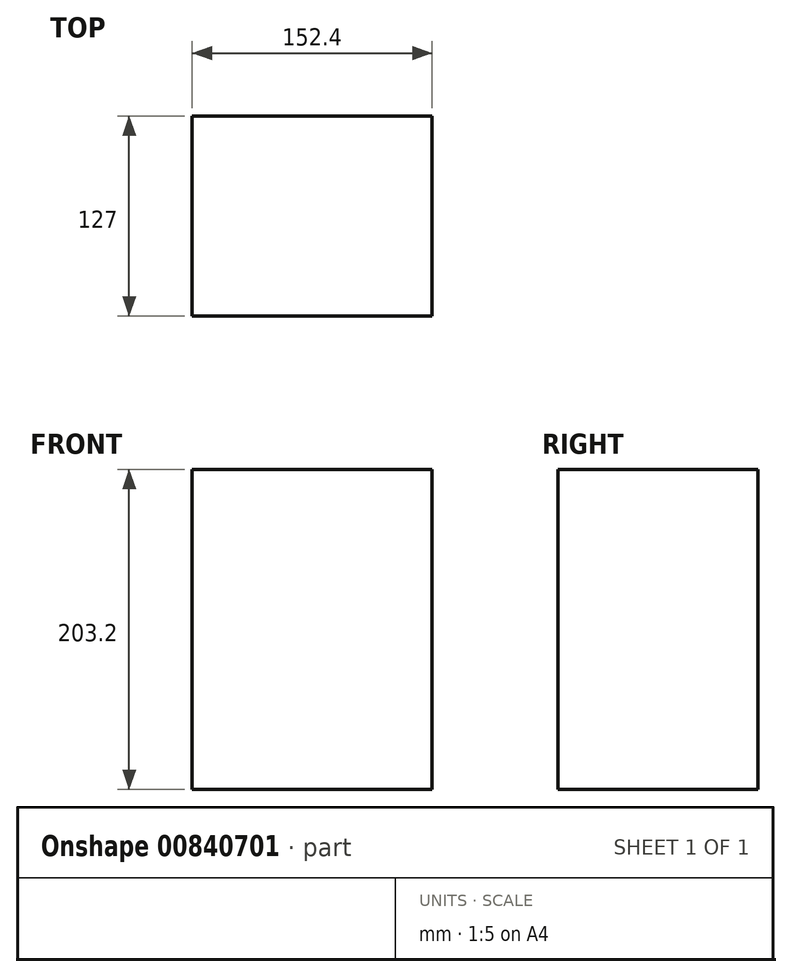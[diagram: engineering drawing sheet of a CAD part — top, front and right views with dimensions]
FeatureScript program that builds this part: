
annotation { "Feature Type Name" : "Feature", "Feature Type Description" : "" }
export const myFeature = defineFeature(function(context is Context, id is Id, definition is map)
    precondition{}
    {
        {
            var Q0;
            Q0=qCreatedBy(makeId("Top.planeOp"),FACE);
            var sketch = newSketch(context, id + "F0", { "sketchPlane" : qUnion([Q0])});
            skLineSegment(sketch, "E0.bottom", {"start": v(-76.2, 63.5) * mm, "end": v(76.2, 63.5) * mm});
            skLineSegment(sketch, "E0.top", {"start": v(-76.2, -63.5) * mm, "end": v(76.2, -63.5) * mm});
            skLineSegment(sketch, "E0.left", {"start": v(-76.2, 63.5) * mm, "end": v(-76.2, -63.5) * mm});
            skLineSegment(sketch, "E0.right", {"start": v(76.2, 63.5) * mm, "end": v(76.2, -63.5) * mm});
            skPoint(sketch, "E0.middle", {"position": v(0, 0) * mm});
            skSolve(sketch);
        }
        {
            var Q0;
            Q0=makeQuery(id+"F0.imprint","IMPRINT",FACE,{"disambiguationData":[TD([[makeQuery(id+"F0.imprint","IMPRINT",EDGE,{"derivedFrom":sQuery(id+"F0.wireOp",EDGE,"E0.bottom")}),-1.0]])]});
            extrude(context, id + "F1", {"entities" : qUnion([Q0]), "depth" : 203.2 * mm, "offsetDistance" : 25.4 * mm});
        }
    });
